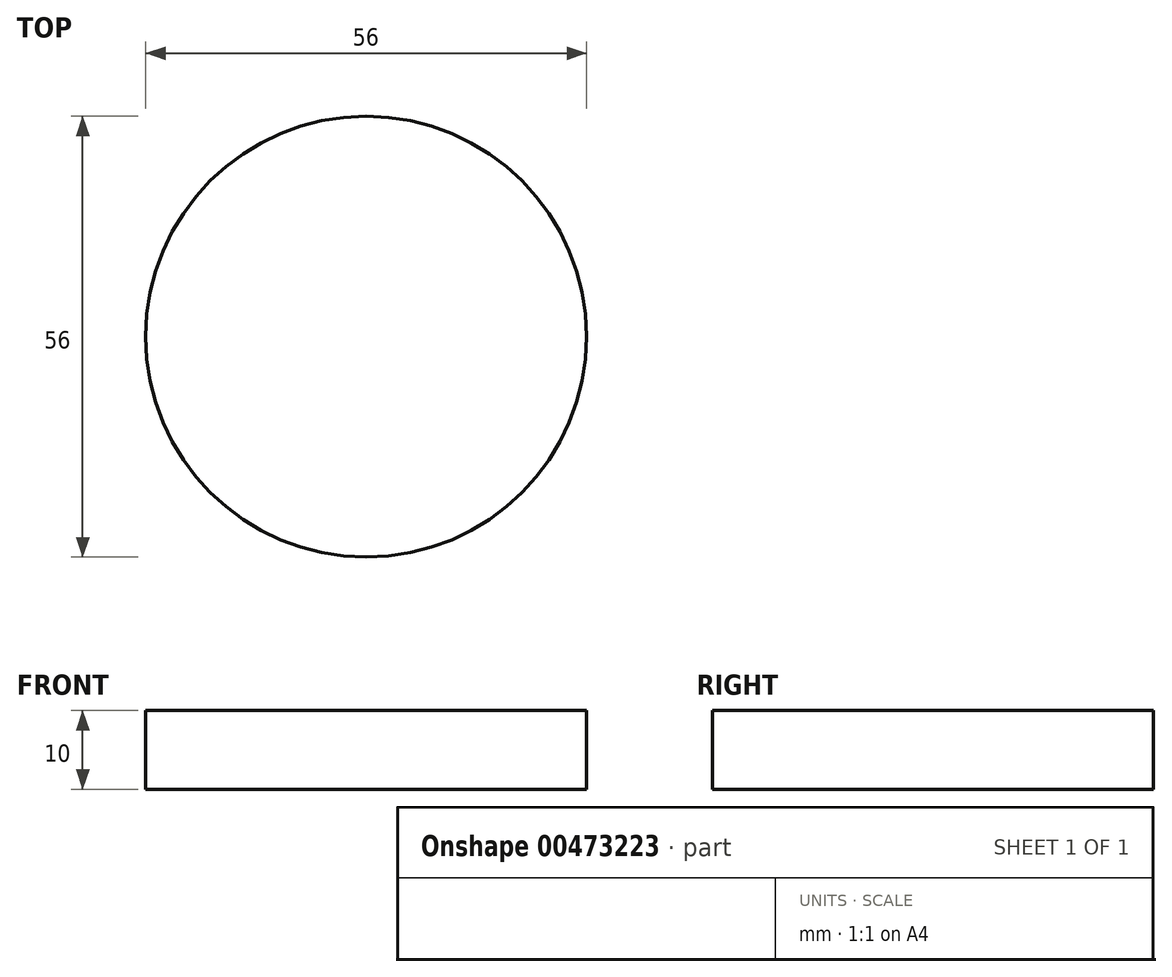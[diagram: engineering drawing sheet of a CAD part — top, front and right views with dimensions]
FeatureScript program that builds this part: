
annotation { "Feature Type Name" : "Feature", "Feature Type Description" : "" }
export const myFeature = defineFeature(function(context is Context, id is Id, definition is map)
    precondition{}
    {
        {
            var Q0;
            Q0=qCreatedBy(makeId("Top.planeOp"),FACE);
            var sketch = newSketch(context, id + "F0", { "sketchPlane" : qUnion([Q0])});
            skCircle(sketch, "E0", {"center": v(-46.3, 17.12) * mm, "radius": 27.5 * mm});
            skCircle(sketch, "E1", {"center": v(-46.3, 17.12) * mm, "radius": 28 * mm});
            skSolve(sketch);
        }
        {
            var Q0;
            Q0=sQuery(id+"F0.wireOp",EDGE,"E1");
            var Q1;
            Q1=sQuery(id+"F0.wireOp",EDGE,"E0");
            extrude(context, id + "F1", {"bodyType" : ToolBodyType.SURFACE, "surfaceEntities" : qUnion([Q0, Q1]), "depth" : 50 * mm});
        }
        {
            var Q0;
            Q0=qCreatedBy(makeId("Top.planeOp"),FACE);
            var sketch = newSketch(context, id + "F2", { "sketchPlane" : qUnion([Q0])});
            skCircle(sketch, "E2", {"center": v(-46.3, 17.12) * mm, "radius": 28 * mm});
            skSolve(sketch);
        }
        {
            var Q0;
            Q0=qSketchRegion(id+"F2",true);
            extrude(context, id + "F3", {"entities" : qUnion([Q0]), "depth" : 10 * mm});
        }
    });
